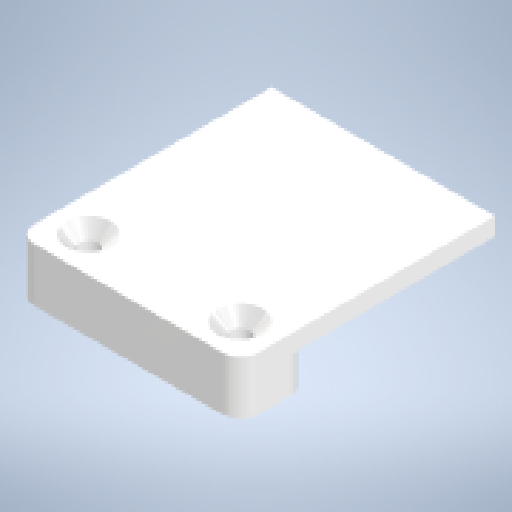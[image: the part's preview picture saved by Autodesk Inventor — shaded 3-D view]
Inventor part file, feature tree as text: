
AUTODESK INVENTOR PART (.ipt)
format: ipt  version: 2025 (Build 290162010, 162A)  size: 228,352 bytes
history: native  units: mm
features: sketch x5, extrude x3, hole x2, fillet x1
ambient origin geometry x8: Origin, YZ Plane, XZ Plane, XY Plane, X Axis, Y Axis, Z Axis, Center Point
bodies: Volumenkörper1 (feature_tree)
feature tree (11):
  extrude  "Extrusion1"  Depth=25.0mm
  extrude  "Extrusion2"  Depth=3.0mm TaperAngle=0.0deg
  hole  "Bohrung1"  [1 undecoded]
  fillet  "Rundung1"  Radius=4.0mm
  extrude  "Extrusion3"  Depth=5.0mm
  hole  "Bohrung2"  [1 undecoded]
  sketch  "Skizze1"  dims[d1=7.5mm d2=25.0mm]
  sketch  "Skizze2"  dims[d4=4.0mm d5=0.0mm d6=3.0mm d7=0.0mm]
  sketch  "Skizze3"  dims[d8=2.2mm d9=6.0mm d10=5.0mm d11=2.0mm d12=90.0deg d13=8.0mm d14=20.594885mm d25=28.5mm d26=4.0mm]
  sketch  "Skizze4"  dims[d27=2.0mm d28=5.0mm]
  sketch  "Skizze5"  dims[d29=5.0mm d30=5.0mm d31=6.0mm d32=2.0mm d33=0.0mm d34=2.5mm d35=2.2mm d36=6.0mm d37=4.4mm d38=2.0mm d39=90.0deg d40=8.0mm d41=20.594885mm d42=2.5mm d43=2.5mm]
note: 2 required parameter values undecoded (feature->parameter linkage not recoverable at this tier; creation-order binding heuristic only, values carry confidence <= 0.55)
